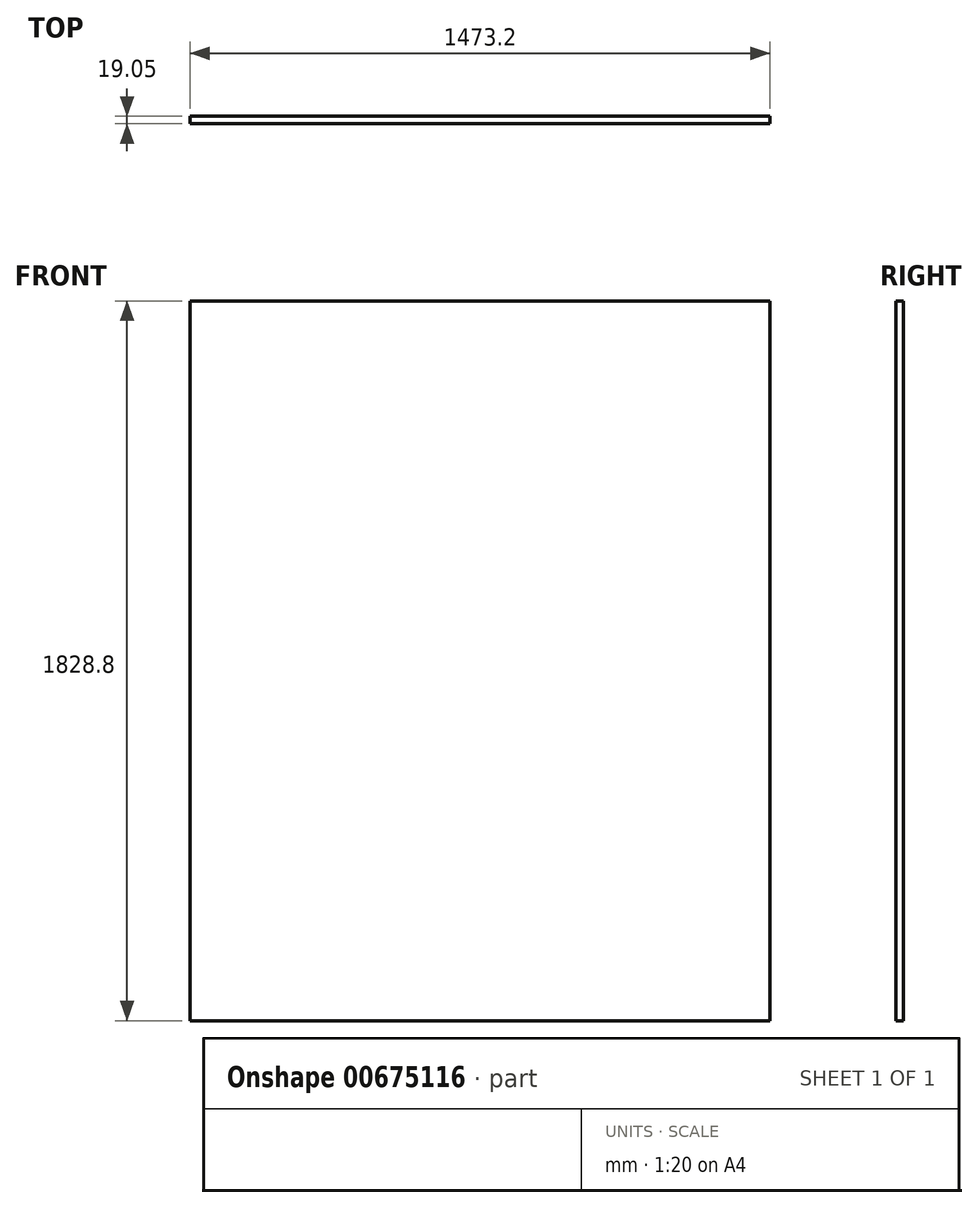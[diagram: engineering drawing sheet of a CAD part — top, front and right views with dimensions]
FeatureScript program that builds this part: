
annotation { "Feature Type Name" : "Feature", "Feature Type Description" : "" }
export const myFeature = defineFeature(function(context is Context, id is Id, definition is map)
    precondition{}
    {
        {
            var Q0;
            Q0=qCreatedBy(makeId("Front.planeOp"),FACE);
            var sketch = newSketch(context, id + "F0", { "sketchPlane" : qUnion([Q0])});
            skLineSegment(sketch, "E0.bottom", {"start": v(736.6, 914.4) * mm, "end": v(-736.6, 914.4) * mm});
            skLineSegment(sketch, "E0.top", {"start": v(736.6, -914.4) * mm, "end": v(-736.6, -914.4) * mm});
            skLineSegment(sketch, "E0.left", {"start": v(736.6, 914.4) * mm, "end": v(736.6, -914.4) * mm});
            skLineSegment(sketch, "E0.right", {"start": v(-736.6, 914.4) * mm, "end": v(-736.6, -914.4) * mm});
            skPoint(sketch, "E0.middle", {"position": v(0, 0) * mm});
            skSolve(sketch);
        }
        {
            var Q0;
            Q0=makeQuery(id+"F0.imprint","IMPRINT",FACE,{"disambiguationData":[TD([[makeQuery(id+"F0.imprint","IMPRINT",EDGE,{"derivedFrom":sQuery(id+"F0.wireOp",EDGE,"E0.bottom")}),1.0]])]});
            extrude(context, id + "F1", {"entities" : qUnion([Q0]), "depth" : 19.05 * mm, "offsetDistance" : 25.4 * mm});
        }
    });
